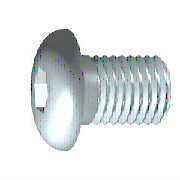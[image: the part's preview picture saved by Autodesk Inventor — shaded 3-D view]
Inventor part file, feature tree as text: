
AUTODESK INVENTOR PART (.ipt)
format: ipt  version: 2021 (Build 250183000, 183)  size: 199,168 bytes
history: native  units: mm (DEFAULTED — no unit token found)
features: sketch x2, extrude x1, plane x1
ambient origin geometry x7: Origin, YZ Plane, XY Plane, X Axis, Y Axis, Z Axis, Center Point
bodies: Solid1 (feature_tree), Body (feature_tree)
feature tree (4):
  extrude  "Slot"  Depth=0.306725mm
  plane  "Work Plane1"
  sketch  "Sketch1"  dims[d0=7.0mm d1=0.306725mm]
  sketch  "Sketch2"  dims[d2=1.65mm d3=1.04mm d4=60.0deg d5=3.0mm d6=3.0mm d7=2.309401mm d8=5.7mm d10=90.0deg d11=10.0mm d9=0.0mm d12=7.0mm d13=0.0mm d14=0.306725mm d15=0.306725mm d16=1.27mm d17=0.0mm d18=0.0mm d19=8.0mm d27=45.0deg d28=0.1mm d29=0.1mm]
